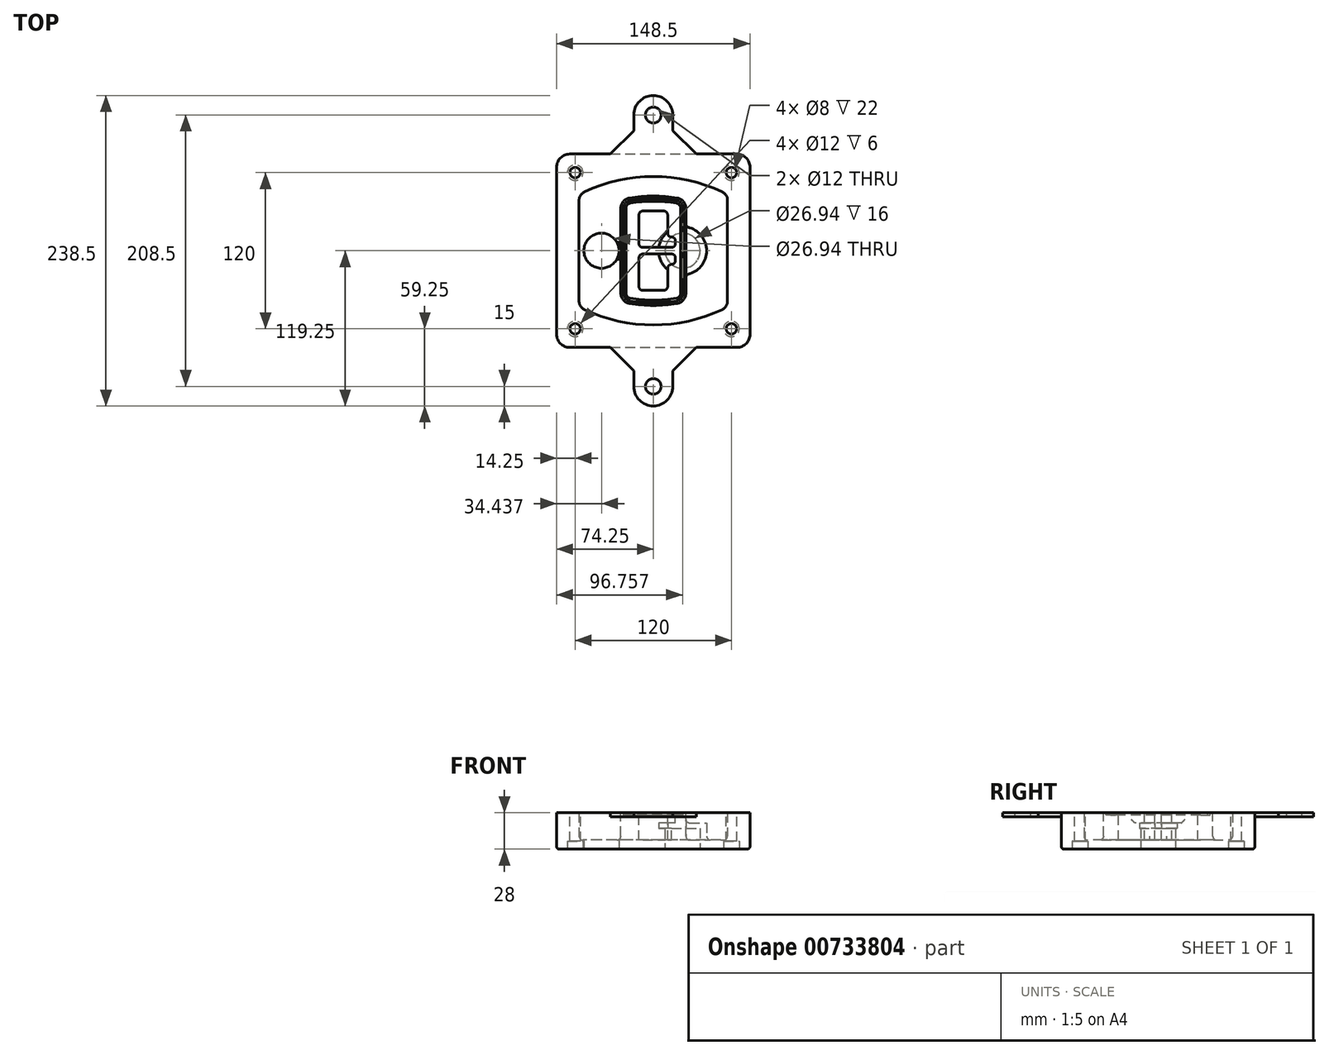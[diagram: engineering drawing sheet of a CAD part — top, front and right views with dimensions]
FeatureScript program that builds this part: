
annotation { "Feature Type Name" : "Feature", "Feature Type Description" : "" }
export const myFeature = defineFeature(function(context is Context, id is Id, definition is map)
    precondition{}
    {
        {
            var Q0;
            Q0=qCreatedBy(makeId("Top.planeOp"),FACE);
            var sketch = newSketch(context, id + "F0", { "sketchPlane" : qUnion([Q0])});
            skPoint(sketch, "E0.rect.middle", {"position": v(0, 0) * mm});
            skLineSegment(sketch, "E1.bottom", {"start": v(-64.25, -74.25) * mm, "end": v(64.25, -74.25) * mm});
            skLineSegment(sketch, "E1.top", {"start": v(-64.25, 74.25) * mm, "end": v(64.25, 74.25) * mm});
            skLineSegment(sketch, "E1.left", {"start": v(-74.25, -64.25) * mm, "end": v(-74.25, 64.25) * mm});
            skLineSegment(sketch, "E1.right", {"start": v(74.25, -64.25) * mm, "end": v(74.25, 64.25) * mm});
            skLineSegment(sketch, "E2", {"start": v(-74.25, 74.25) * mm, "end": v(74.25, -74.25) * mm, "construction": true});
            skLineSegment(sketch, "E3", {"start": v(74.25, 74.25) * mm, "end": v(-74.25, -74.25) * mm, "construction": true});
            skCircle(sketch, "E4", {"center": v(-60, 60) * mm, "radius": 4 * mm});
            skCircle(sketch, "E5", {"center": v(60, 60) * mm, "radius": 4 * mm});
            skCircle(sketch, "E6", {"center": v(60, -60) * mm, "radius": 4 * mm});
            skCircle(sketch, "E7", {"center": v(-60, -60) * mm, "radius": 4 * mm});
            skLineSegment(sketch, "E8", {"start": v(-60, 60) * mm, "end": v(60, 60) * mm, "construction": true});
            skLineSegment(sketch, "E9", {"start": v(60, 60) * mm, "end": v(60, -60) * mm, "construction": true});
            skLineSegment(sketch, "E10", {"start": v(60, -60) * mm, "end": v(-60, -60) * mm, "construction": true});
            skLineSegment(sketch, "E11", {"start": v(-60, -60) * mm, "end": v(-60, 60) * mm, "construction": true});
            skLineSegment(sketch, "E12", {"start": v(-60, 38.83) * mm, "end": v(-60, -38.83) * mm});
            skLineSegment(sketch, "E13", {"start": v(60, 38.83) * mm, "end": v(60, -38.83) * mm});
            skArc(sketch, "E14", {"start": v(54.26, 47.88) * mm, "mid": v(0, 60) * mm, "end": v(-54.26, 47.88) * mm});
            skArc(sketch, "E15", {"start": v(-54.26, -47.88) * mm, "mid": v(0, -60) * mm, "end": v(54.26, -47.88) * mm});
            skLineSegment(sketch, "E16", {"start": v(-60, 0) * mm, "end": v(60, 0) * mm, "construction": true});
            skPoint(sketch, "E17.visualSharp", {"position": v(-60, -45) * mm});
            skArc(sketch, "E17.filletArc", {"start": v(-60, -38.83) * mm, "mid": v(-58.44, -44.2) * mm, "end": v(-54.26, -47.88) * mm});
            skPoint(sketch, "E18.visualSharp", {"position": v(-60, 45) * mm});
            skArc(sketch, "E18.filletArc", {"start": v(-54.26, 47.88) * mm, "mid": v(-58.44, 44.2) * mm, "end": v(-60, 38.83) * mm});
            skPoint(sketch, "E19.visualSharp", {"position": v(60, 45) * mm});
            skArc(sketch, "E19.filletArc", {"start": v(60, 38.83) * mm, "mid": v(58.44, 44.2) * mm, "end": v(54.26, 47.88) * mm});
            skPoint(sketch, "E20.visualSharp", {"position": v(60, -45) * mm});
            skArc(sketch, "E20.filletArc", {"start": v(54.26, -47.88) * mm, "mid": v(58.44, -44.2) * mm, "end": v(60, -38.83) * mm});
            skPoint(sketch, "E21.visualSharp", {"position": v(-74.25, 74.25) * mm});
            skArc(sketch, "E21.filletArc", {"start": v(-64.25, 74.25) * mm, "mid": v(-71.32, 71.32) * mm, "end": v(-74.25, 64.25) * mm});
            skPoint(sketch, "E22.visualSharp", {"position": v(74.25, 74.25) * mm});
            skArc(sketch, "E22.filletArc", {"start": v(74.25, 64.25) * mm, "mid": v(71.32, 71.32) * mm, "end": v(64.25, 74.25) * mm});
            skPoint(sketch, "E23.visualSharp", {"position": v(74.25, -74.25) * mm});
            skArc(sketch, "E23.filletArc", {"start": v(64.25, -74.25) * mm, "mid": v(71.32, -71.32) * mm, "end": v(74.25, -64.25) * mm});
            skPoint(sketch, "E24.visualSharp", {"position": v(-74.25, -74.25) * mm});
            skArc(sketch, "E24.filletArc", {"start": v(-74.25, -64.25) * mm, "mid": v(-71.32, -71.32) * mm, "end": v(-64.25, -74.25) * mm});
            skArc(sketch, "E25.0", {"start": v(57, 38.83) * mm, "mid": v(55.9, 42.58) * mm, "end": v(52.98, 45.17) * mm});
            skLineSegment(sketch, "E25.1", {"start": v(57, 38.83) * mm, "end": v(57, -38.83) * mm});
            skArc(sketch, "E25.2", {"start": v(52.98, -45.17) * mm, "mid": v(55.9, -42.58) * mm, "end": v(57, -38.83) * mm});
            skArc(sketch, "E25.3", {"start": v(-52.98, -45.17) * mm, "mid": v(0, -57) * mm, "end": v(52.98, -45.17) * mm});
            skArc(sketch, "E25.4", {"start": v(-57, -38.83) * mm, "mid": v(-55.9, -42.58) * mm, "end": v(-52.98, -45.17) * mm});
            skArc(sketch, "E25.5", {"start": v(52.98, 45.17) * mm, "mid": v(0, 57) * mm, "end": v(-52.98, 45.17) * mm});
            skLineSegment(sketch, "E25.6", {"start": v(-57, 38.83) * mm, "end": v(-57, -38.83) * mm});
            skArc(sketch, "E25.7", {"start": v(-52.98, 45.17) * mm, "mid": v(-55.9, 42.58) * mm, "end": v(-57, 38.83) * mm});
            skArc(sketch, "E26.0", {"start": v(-55.96, 51.5) * mm, "mid": v(-61.82, 46.33) * mm, "end": v(-64, 38.83) * mm});
            skArc(sketch, "E26.1", {"start": v(55.96, 51.5) * mm, "mid": v(0, 64) * mm, "end": v(-55.96, 51.5) * mm});
            skArc(sketch, "E26.2", {"start": v(64, 38.83) * mm, "mid": v(61.82, 46.33) * mm, "end": v(55.96, 51.5) * mm});
            skLineSegment(sketch, "E26.3", {"start": v(64, 38.83) * mm, "end": v(64, -38.83) * mm});
            skArc(sketch, "E26.4", {"start": v(55.96, -51.5) * mm, "mid": v(61.82, -46.33) * mm, "end": v(64, -38.83) * mm});
            skLineSegment(sketch, "E26.5", {"start": v(-64, 38.83) * mm, "end": v(-64, -38.83) * mm});
            skArc(sketch, "E26.6", {"start": v(-55.96, -51.5) * mm, "mid": v(0, -64) * mm, "end": v(55.96, -51.5) * mm});
            skArc(sketch, "E26.7", {"start": v(-64, -38.83) * mm, "mid": v(-61.82, -46.33) * mm, "end": v(-55.96, -51.5) * mm});
            skSolve(sketch);
        }
        {
            var Q0;
            Q0=makeQuery(id+"F0.imprint","IMPRINT",FACE,{"disambiguationData":[TD([[makeQuery(id+"F0.imprint","IMPRINT",EDGE,{"derivedFrom":sQuery(id+"F0.wireOp",EDGE,"E1.bottom")}),1.0]])]});
            var Q1;
            Q1=makeQuery(id+"F0.imprint","IMPRINT",FACE,{"disambiguationData":[TD([[makeQuery(id+"F0.imprint","IMPRINT",EDGE,{"derivedFrom":sQuery(id+"F0.wireOp",EDGE,"E12")}),1.0]])]});
            var Q2;
            Q2=makeQuery(id+"F0.imprint","IMPRINT",FACE,{"disambiguationData":[TD([[makeQuery(id+"F0.imprint","IMPRINT",EDGE,{"derivedFrom":sQuery(id+"F0.wireOp",EDGE,"E25.0")}),1.0]])]});
            var Q3;
            Q3=makeQuery(id+"F0.imprint","IMPRINT",FACE,{"disambiguationData":[TD([[makeQuery(id+"F0.imprint","IMPRINT",EDGE,{"derivedFrom":sQuery(id+"F0.wireOp",EDGE,"E12")}),-1.0]])]});
            extrude(context, id + "F1", {"entities" : qUnion([Q0, Q1, Q2, Q3]), "oppositeDirection" : true, "depth" : 25 * mm});
        }
        {
            var Q0;
            Q0=makeQuery(id+"F0.imprint","IMPRINT",FACE,{"disambiguationData":[TD([[makeQuery(id+"F0.imprint","IMPRINT",EDGE,{"derivedFrom":sQuery(id+"F0.wireOp",EDGE,"E12")}),1.0]])]});
            extrude(context, id + "F2", {"entities" : qUnion([Q0]), "operationType" : NewBodyOperationType.ADD, "depth" : 3 * mm});
        }
        {
            var Q0;
            Q0=makeQuery(id+"F0.imprint","IMPRINT",FACE,{"disambiguationData":[TD([[makeQuery(id+"F0.imprint","IMPRINT",EDGE,{"derivedFrom":sQuery(id+"F0.wireOp",EDGE,"E25.0")}),1.0]])]});
            extrude(context, id + "F3", {"entities" : qUnion([Q0]), "operationType" : NewBodyOperationType.REMOVE, "oppositeDirection" : true, "depth" : 18 * mm});
        }
        {
            var Q0;
            Q0=makeQuery(id+"F2.opExtrude","CAP_FACE",FACE,{"disambiguationData":[OSD([sQuery(id+"F0.wireOp",EDGE,"E12"),sQuery(id+"F0.wireOp",EDGE,"E13"),sQuery(id+"F0.wireOp",EDGE,"E14"),sQuery(id+"F0.wireOp",EDGE,"E15"),sQuery(id+"F0.wireOp",EDGE,"E17.filletArc"),sQuery(id+"F0.wireOp",EDGE,"E18.filletArc"),sQuery(id+"F0.wireOp",EDGE,"E19.filletArc"),sQuery(id+"F0.wireOp",EDGE,"E20.filletArc"),sQuery(id+"F0.wireOp",EDGE,"E25.0"),sQuery(id+"F0.wireOp",EDGE,"E25.1"),sQuery(id+"F0.wireOp",EDGE,"E25.2"),sQuery(id+"F0.wireOp",EDGE,"E25.3"),sQuery(id+"F0.wireOp",EDGE,"E25.4"),sQuery(id+"F0.wireOp",EDGE,"E25.5"),sQuery(id+"F0.wireOp",EDGE,"E25.6"),sQuery(id+"F0.wireOp",EDGE,"E25.7")])],"isStart":false});
            var sketch = newSketch(context, id + "F4", { "sketchPlane" : qUnion([Q0])});
            skArc(sketch, "E27.0", {"start": v(-18.34, -40.45) * mm, "mid": v(0, -42) * mm, "end": v(18.34, -40.45) * mm});
            skArc(sketch, "E28.0", {"start": v(18.34, 40.45) * mm, "mid": v(0, 42) * mm, "end": v(-18.34, 40.45) * mm});
            skLineSegment(sketch, "E29", {"start": v(-25, 32.57) * mm, "end": v(-25, -32.57) * mm});
            skLineSegment(sketch, "E30", {"start": v(25, 32.57) * mm, "end": v(25, -32.57) * mm});
            skLineSegment(sketch, "E31", {"start": v(-25, 39.1) * mm, "end": v(25, 39.1) * mm, "construction": true});
            skLineSegment(sketch, "E32", {"start": v(-25, -39.1) * mm, "end": v(25, -39.1) * mm, "construction": true});
            skPoint(sketch, "E33.visualSharp", {"position": v(-25, 39.1) * mm});
            skArc(sketch, "E33.filletArc", {"start": v(-18.34, 40.45) * mm, "mid": v(-23.11, 37.73) * mm, "end": v(-25, 32.57) * mm});
            skPoint(sketch, "E34.visualSharp", {"position": v(25, 39.1) * mm});
            skArc(sketch, "E34.filletArc", {"start": v(25, 32.57) * mm, "mid": v(23.11, 37.73) * mm, "end": v(18.34, 40.45) * mm});
            skPoint(sketch, "E35.visualSharp", {"position": v(25, -39.1) * mm});
            skArc(sketch, "E35.filletArc", {"start": v(18.34, -40.45) * mm, "mid": v(23.11, -37.73) * mm, "end": v(25, -32.57) * mm});
            skPoint(sketch, "E36.visualSharp", {"position": v(-25, -39.1) * mm});
            skArc(sketch, "E36.filletArc", {"start": v(-25, -32.57) * mm, "mid": v(-23.11, -37.73) * mm, "end": v(-18.34, -40.45) * mm});
            skArc(sketch, "E37.0", {"start": v(52.98, 45.17) * mm, "mid": v(0, 57) * mm, "end": v(-52.98, 45.17) * mm});
            skArc(sketch, "E37.1", {"start": v(-52.98, 45.17) * mm, "mid": v(-55.9, 42.58) * mm, "end": v(-57, 38.83) * mm});
            skLineSegment(sketch, "E37.2", {"start": v(-57, 38.83) * mm, "end": v(-57, -38.83) * mm});
            skArc(sketch, "E37.3", {"start": v(-57, -38.83) * mm, "mid": v(-55.9, -42.58) * mm, "end": v(-52.98, -45.17) * mm});
            skArc(sketch, "E37.4", {"start": v(-52.98, -45.17) * mm, "mid": v(0, -57) * mm, "end": v(52.98, -45.17) * mm});
            skArc(sketch, "E37.5", {"start": v(52.98, -45.17) * mm, "mid": v(55.9, -42.58) * mm, "end": v(57, -38.83) * mm});
            skLineSegment(sketch, "E37.6", {"start": v(57, 38.83) * mm, "end": v(57, -38.83) * mm});
            skArc(sketch, "E37.7", {"start": v(57, 38.83) * mm, "mid": v(55.9, 42.58) * mm, "end": v(52.98, 45.17) * mm});
            skLineSegment(sketch, "E38.0", {"start": v(23, 32.57) * mm, "end": v(23, -32.57) * mm});
            skArc(sketch, "E38.1", {"start": v(18, -38.48) * mm, "mid": v(21.58, -36.44) * mm, "end": v(23, -32.57) * mm});
            skArc(sketch, "E38.2", {"start": v(-18, -38.48) * mm, "mid": v(0, -40) * mm, "end": v(18, -38.48) * mm});
            skArc(sketch, "E38.3", {"start": v(-23, -32.57) * mm, "mid": v(-21.58, -36.44) * mm, "end": v(-18, -38.48) * mm});
            skLineSegment(sketch, "E38.4", {"start": v(-23, 32.57) * mm, "end": v(-23, -32.57) * mm});
            skArc(sketch, "E38.5", {"start": v(23, 32.57) * mm, "mid": v(21.58, 36.44) * mm, "end": v(18, 38.48) * mm});
            skArc(sketch, "E38.6", {"start": v(-18, 38.48) * mm, "mid": v(-21.58, 36.44) * mm, "end": v(-23, 32.57) * mm});
            skArc(sketch, "E38.7", {"start": v(18, 38.48) * mm, "mid": v(0, 40) * mm, "end": v(-18, 38.48) * mm});
            skArc(sketch, "E39.0", {"start": v(21, 32.57) * mm, "mid": v(20.06, 35.15) * mm, "end": v(17.67, 36.5) * mm});
            skLineSegment(sketch, "E39.1", {"start": v(21, 32.57) * mm, "end": v(21, -32.57) * mm});
            skArc(sketch, "E39.2", {"start": v(17.67, -36.5) * mm, "mid": v(20.06, -35.15) * mm, "end": v(21, -32.57) * mm});
            skArc(sketch, "E39.3", {"start": v(-17.67, -36.5) * mm, "mid": v(0, -38) * mm, "end": v(17.67, -36.5) * mm});
            skArc(sketch, "E39.4", {"start": v(-21, -32.57) * mm, "mid": v(-20.06, -35.15) * mm, "end": v(-17.67, -36.5) * mm});
            skArc(sketch, "E39.5", {"start": v(17.67, 36.5) * mm, "mid": v(0, 38) * mm, "end": v(-17.67, 36.5) * mm});
            skLineSegment(sketch, "E39.6", {"start": v(-21, 32.57) * mm, "end": v(-21, -32.57) * mm});
            skArc(sketch, "E39.7", {"start": v(-17.67, 36.5) * mm, "mid": v(-20.06, 35.15) * mm, "end": v(-21, 32.57) * mm});
            skLineSegment(sketch, "E40", {"start": v(-25, 0) * mm, "end": v(25, 0) * mm, "construction": true});
            skLineSegment(sketch, "E41", {"start": v(-11, 5.5) * mm, "end": v(-11, 27.5) * mm});
            skLineSegment(sketch, "E42", {"start": v(-8, 30.5) * mm, "end": v(8, 30.5) * mm});
            skLineSegment(sketch, "E43", {"start": v(11, 27.5) * mm, "end": v(11, 13.5) * mm});
            skLineSegment(sketch, "E44", {"start": v(14, 10.5) * mm, "end": v(14, 10.5) * mm});
            skLineSegment(sketch, "E45", {"start": v(17, 7.5) * mm, "end": v(17, 5.5) * mm});
            skLineSegment(sketch, "E46", {"start": v(14, 2.5) * mm, "end": v(-8, 2.5) * mm});
            skPoint(sketch, "E47.visualSharp", {"position": v(-11, 30.5) * mm});
            skArc(sketch, "E47.filletArc", {"start": v(-8, 30.5) * mm, "mid": v(-10.12, 29.62) * mm, "end": v(-11, 27.5) * mm});
            skPoint(sketch, "E48.visualSharp", {"position": v(11, 30.5) * mm});
            skArc(sketch, "E48.filletArc", {"start": v(11, 27.5) * mm, "mid": v(10.12, 29.62) * mm, "end": v(8, 30.5) * mm});
            skPoint(sketch, "E49.visualSharp", {"position": v(11, 10.5) * mm});
            skArc(sketch, "E49.filletArc", {"start": v(11, 13.5) * mm, "mid": v(11.88, 11.38) * mm, "end": v(14, 10.5) * mm});
            skPoint(sketch, "E50.visualSharp", {"position": v(17, 10.5) * mm});
            skArc(sketch, "E50.filletArc", {"start": v(17, 7.5) * mm, "mid": v(16.12, 9.62) * mm, "end": v(14, 10.5) * mm});
            skPoint(sketch, "E51.visualSharp", {"position": v(17, 2.5) * mm});
            skArc(sketch, "E51.filletArc", {"start": v(14, 2.5) * mm, "mid": v(16.12, 3.38) * mm, "end": v(17, 5.5) * mm});
            skPoint(sketch, "E52.visualSharp", {"position": v(-11, 2.5) * mm});
            skArc(sketch, "E52.filletArc", {"start": v(-11, 5.5) * mm, "mid": v(-10.12, 3.38) * mm, "end": v(-8, 2.5) * mm});
            skLineSegment(sketch, "E53.0.MirrorCS", {"start": v(14, -2.5) * mm, "end": v(-8, -2.5) * mm});
            skArc(sketch, "E54.0.MirrorCS", {"start": v(-11, -5.5) * mm, "mid": v(-10.12, -3.38) * mm, "end": v(-8, -2.5) * mm});
            skLineSegment(sketch, "E55.0.MirrorCS", {"start": v(-11, -5.5) * mm, "end": v(-11, -27.5) * mm});
            skArc(sketch, "E56.0.MirrorCS", {"start": v(-8, -30.5) * mm, "mid": v(-10.12, -29.62) * mm, "end": v(-11, -27.5) * mm});
            skLineSegment(sketch, "E57.0.MirrorCS", {"start": v(-8, -30.5) * mm, "end": v(8, -30.5) * mm});
            skArc(sketch, "E58.0.MirrorCS", {"start": v(11, -27.5) * mm, "mid": v(10.12, -29.62) * mm, "end": v(8, -30.5) * mm});
            skLineSegment(sketch, "E59.0.MirrorCS", {"start": v(11, -27.5) * mm, "end": v(11, -13.5) * mm});
            skArc(sketch, "E60.0.MirrorCS", {"start": v(11, -13.5) * mm, "mid": v(11.88, -11.38) * mm, "end": v(14, -10.5) * mm});
            skArc(sketch, "E61.0.MirrorCS", {"start": v(17, -7.5) * mm, "mid": v(16.12, -9.62) * mm, "end": v(14, -10.5) * mm});
            skLineSegment(sketch, "E62.0.MirrorCS", {"start": v(17, -7.5) * mm, "end": v(17, -5.5) * mm});
            skArc(sketch, "E63.0.MirrorCS", {"start": v(14, -2.5) * mm, "mid": v(16.12, -3.38) * mm, "end": v(17, -5.5) * mm});
            skSolve(sketch);
        }
        {
            var Q0;
            Q0=makeQuery(id+"F4.imprint","IMPRINT",FACE,{"disambiguationData":[TD([[makeQuery(id+"F4.imprint","IMPRINT",EDGE,{"derivedFrom":sQuery(id+"F4.wireOp",EDGE,"E27.0")}),1.0]])]});
            var Q1;
            Q1=makeQuery(id+"F4.imprint","IMPRINT",FACE,{"disambiguationData":[TD([[makeQuery(id+"F4.imprint","IMPRINT",EDGE,{"derivedFrom":sQuery(id+"F4.wireOp",EDGE,"E38.0")}),-1.0]])]});
            var Q2;
            Q2=makeQuery(id+"F4.imprint","IMPRINT",FACE,{"disambiguationData":[TD([[makeQuery(id+"F4.imprint","IMPRINT",EDGE,{"derivedFrom":sQuery(id+"F4.wireOp",EDGE,"E39.0")}),1.0]])]});
            extrude(context, id + "F5", {"entities" : qUnion([Q0, Q1, Q2]), "operationType" : NewBodyOperationType.ADD, "endBound" : BoundingType.UP_TO_NEXT, "oppositeDirection" : true, "depth" : 25 * mm});
        }
        {
            var Q0;
            Q0=makeQuery(id+"F4.imprint","IMPRINT",FACE,{"disambiguationData":[TD([[makeQuery(id+"F4.imprint","IMPRINT",EDGE,{"derivedFrom":sQuery(id+"F4.wireOp",EDGE,"E38.0")}),-1.0]])]});
            extrude(context, id + "F6", {"entities" : qUnion([Q0]), "operationType" : NewBodyOperationType.REMOVE, "oppositeDirection" : true, "depth" : 2 * mm});
        }
        {
            var Q0;
            Q0=makeQuery(id+"F1.opExtrude","CAP_FACE",FACE,{"disambiguationData":[OSD([sQuery(id+"F0.wireOp",EDGE,"E1.bottom"),sQuery(id+"F0.wireOp",EDGE,"E1.top"),sQuery(id+"F0.wireOp",EDGE,"E1.left"),sQuery(id+"F0.wireOp",EDGE,"E1.right"),sQuery(id+"F0.wireOp",EDGE,"E4"),sQuery(id+"F0.wireOp",EDGE,"E5"),sQuery(id+"F0.wireOp",EDGE,"E6"),sQuery(id+"F0.wireOp",EDGE,"E7"),sQuery(id+"F0.wireOp",EDGE,"E21.filletArc"),sQuery(id+"F0.wireOp",EDGE,"E22.filletArc"),sQuery(id+"F0.wireOp",EDGE,"E23.filletArc"),sQuery(id+"F0.wireOp",EDGE,"E24.filletArc")])],"isStart":false});
            var sketch = newSketch(context, id + "F7", { "sketchPlane" : qUnion([Q0])});
            skCircle(sketch, "E64", {"center": v(22.5, 0) * mm, "radius": 13.47 * mm});
            skCircle(sketch, "E65", {"center": v(-39.81, 0) * mm, "radius": 13.47 * mm});
            skLineSegment(sketch, "E66", {"start": v(74.25, 0) * mm, "end": v(-74.25, 0) * mm});
            skCircle(sketch, "E67", {"center": v(22.5, 0) * mm, "radius": 18.47 * mm});
            skCircle(sketch, "E68", {"center": v(60, -60) * mm, "radius": 6 * mm});
            skCircle(sketch, "E69", {"center": v(-60, -60) * mm, "radius": 6 * mm});
            skCircle(sketch, "E70", {"center": v(-60, 60) * mm, "radius": 6 * mm});
            skCircle(sketch, "E71", {"center": v(60, 60) * mm, "radius": 6 * mm});
            skSolve(sketch);
        }
        {
            var Q0;
            {var subQ1=sQuery(id+"F7.wireOp",EDGE,"E66");var subQ4=sQuery(id+"F7.wireOp",EDGE,"E64");var subQ6=makeQuery(id+"F7.imprint","INTERSECT",VERTEX,{"disambiguationData":[OD(0.0)],"derivedFrom":[subQ4,subQ1]});Q0=makeQuery(id+"F7.imprint","IMPRINT",FACE,{"disambiguationData":[TD([[makeQuery(id+"F7.imprint","IMPRINT",EDGE,{"disambiguationData":[TD([[subQ6,-1.0]])],"derivedFrom":subQ4}),-1.0]])]});}
            var Q1;
            {var subQ0=sQuery(id+"F7.wireOp",EDGE,"E66");var subQ1=sQuery(id+"F7.wireOp",EDGE,"E64");var subQ3=makeQuery(id+"F7.imprint","INTERSECT",VERTEX,{"disambiguationData":[OD(0.0)],"derivedFrom":[subQ1,subQ0]});Q1=makeQuery(id+"F7.imprint","IMPRINT",FACE,{"disambiguationData":[TD([[makeQuery(id+"F7.imprint","IMPRINT",EDGE,{"disambiguationData":[TD([[subQ3,-1.0]])],"derivedFrom":subQ1}),1.0]])]});}
            var Q2;
            {var subQ0=sQuery(id+"F7.wireOp",EDGE,"E66");var subQ1=sQuery(id+"F7.wireOp",EDGE,"E64");var subQ3=makeQuery(id+"F7.imprint","INTERSECT",VERTEX,{"disambiguationData":[OD(0.0)],"derivedFrom":[subQ1,subQ0]});Q2=makeQuery(id+"F7.imprint","IMPRINT",FACE,{"disambiguationData":[TD([[makeQuery(id+"F7.imprint","IMPRINT",EDGE,{"disambiguationData":[TD([[subQ3,1.0]])],"derivedFrom":subQ1}),1.0]])]});}
            var Q3;
            {var subQ1=sQuery(id+"F7.wireOp",EDGE,"E66");var subQ4=sQuery(id+"F7.wireOp",EDGE,"E64");var subQ6=makeQuery(id+"F7.imprint","INTERSECT",VERTEX,{"disambiguationData":[OD(0.0)],"derivedFrom":[subQ4,subQ1]});Q3=makeQuery(id+"F7.imprint","IMPRINT",FACE,{"disambiguationData":[TD([[makeQuery(id+"F7.imprint","IMPRINT",EDGE,{"disambiguationData":[TD([[subQ6,1.0]])],"derivedFrom":subQ4}),-1.0]])]});}
            extrude(context, id + "F8", {"entities" : qUnion([Q0, Q1, Q2, Q3]), "operationType" : NewBodyOperationType.ADD, "oppositeDirection" : true, "depth" : 20 * mm});
        }
        {
            var Q0;
            {var subQ0=sQuery(id+"F7.wireOp",EDGE,"E66");var subQ1=sQuery(id+"F7.wireOp",EDGE,"E64");var subQ3=makeQuery(id+"F7.imprint","INTERSECT",VERTEX,{"disambiguationData":[OD(0.0)],"derivedFrom":[subQ1,subQ0]});Q0=makeQuery(id+"F7.imprint","IMPRINT",FACE,{"disambiguationData":[TD([[makeQuery(id+"F7.imprint","IMPRINT",EDGE,{"disambiguationData":[TD([[subQ3,-1.0]])],"derivedFrom":subQ1}),1.0]])]});}
            var Q1;
            {var subQ0=sQuery(id+"F7.wireOp",EDGE,"E66");var subQ1=sQuery(id+"F7.wireOp",EDGE,"E64");var subQ3=makeQuery(id+"F7.imprint","INTERSECT",VERTEX,{"disambiguationData":[OD(0.0)],"derivedFrom":[subQ1,subQ0]});Q1=makeQuery(id+"F7.imprint","IMPRINT",FACE,{"disambiguationData":[TD([[makeQuery(id+"F7.imprint","IMPRINT",EDGE,{"disambiguationData":[TD([[subQ3,1.0]])],"derivedFrom":subQ1}),1.0]])]});}
            extrude(context, id + "F9", {"entities" : qUnion([Q0, Q1]), "operationType" : NewBodyOperationType.REMOVE, "oppositeDirection" : true, "depth" : 16 * mm});
        }
        {
            var Q0;
            {var subQ0=sQuery(id+"F7.wireOp",EDGE,"E66");var subQ1=sQuery(id+"F7.wireOp",EDGE,"E65");var subQ3=makeQuery(id+"F7.imprint","INTERSECT",VERTEX,{"disambiguationData":[OD(0.0)],"derivedFrom":[subQ1,subQ0]});Q0=makeQuery(id+"F7.imprint","IMPRINT",FACE,{"disambiguationData":[TD([[makeQuery(id+"F7.imprint","IMPRINT",EDGE,{"disambiguationData":[TD([[subQ3,-1.0]])],"derivedFrom":subQ1}),1.0]])]});}
            var Q1;
            {var subQ0=sQuery(id+"F7.wireOp",EDGE,"E66");var subQ1=sQuery(id+"F7.wireOp",EDGE,"E65");var subQ3=makeQuery(id+"F7.imprint","INTERSECT",VERTEX,{"disambiguationData":[OD(0.0)],"derivedFrom":[subQ1,subQ0]});Q1=makeQuery(id+"F7.imprint","IMPRINT",FACE,{"disambiguationData":[TD([[makeQuery(id+"F7.imprint","IMPRINT",EDGE,{"disambiguationData":[TD([[subQ3,1.0]])],"derivedFrom":subQ1}),1.0]])]});}
            extrude(context, id + "F10", {"entities" : qUnion([Q0, Q1]), "operationType" : NewBodyOperationType.REMOVE, "oppositeDirection" : true, "depth" : 25 * mm});
        }
        {
            var Q0;
            Q0=makeQuery(id+"F7.imprint","IMPRINT",FACE,{"disambiguationData":[TD([[makeQuery(id+"F7.imprint","IMPRINT",EDGE,{"derivedFrom":sQuery(id+"F7.wireOp",EDGE,"E68")}),1.0]])]});
            var Q1;
            Q1=makeQuery(id+"F7.imprint","IMPRINT",FACE,{"disambiguationData":[TD([[makeQuery(id+"F7.imprint","IMPRINT",EDGE,{"derivedFrom":makeQuery(id+"F1.opExtrude","CAP_EDGE",EDGE,{"disambiguationData":[OSD([sQuery(id+"F0.wireOp",EDGE,"E5")])],"isStart":false})}),-1.0]])]});
            var Q2;
            Q2=makeQuery(id+"F7.imprint","IMPRINT",FACE,{"disambiguationData":[TD([[makeQuery(id+"F7.imprint","IMPRINT",EDGE,{"derivedFrom":sQuery(id+"F7.wireOp",EDGE,"E69")}),1.0]])]});
            var Q3;
            Q3=makeQuery(id+"F7.imprint","IMPRINT",FACE,{"disambiguationData":[TD([[makeQuery(id+"F7.imprint","IMPRINT",EDGE,{"derivedFrom":makeQuery(id+"F1.opExtrude","CAP_EDGE",EDGE,{"disambiguationData":[OSD([sQuery(id+"F0.wireOp",EDGE,"E4")])],"isStart":false})}),-1.0]])]});
            var Q4;
            Q4=makeQuery(id+"F7.imprint","IMPRINT",FACE,{"disambiguationData":[TD([[makeQuery(id+"F7.imprint","IMPRINT",EDGE,{"derivedFrom":sQuery(id+"F7.wireOp",EDGE,"E70")}),1.0]])]});
            var Q5;
            Q5=makeQuery(id+"F7.imprint","IMPRINT",FACE,{"disambiguationData":[TD([[makeQuery(id+"F7.imprint","IMPRINT",EDGE,{"derivedFrom":makeQuery(id+"F1.opExtrude","CAP_EDGE",EDGE,{"disambiguationData":[OSD([sQuery(id+"F0.wireOp",EDGE,"E7")])],"isStart":false})}),-1.0]])]});
            var Q6;
            Q6=makeQuery(id+"F7.imprint","IMPRINT",FACE,{"disambiguationData":[TD([[makeQuery(id+"F7.imprint","IMPRINT",EDGE,{"derivedFrom":sQuery(id+"F7.wireOp",EDGE,"E71")}),1.0]])]});
            var Q7;
            Q7=makeQuery(id+"F7.imprint","IMPRINT",FACE,{"disambiguationData":[TD([[makeQuery(id+"F7.imprint","IMPRINT",EDGE,{"derivedFrom":makeQuery(id+"F1.opExtrude","CAP_EDGE",EDGE,{"disambiguationData":[OSD([sQuery(id+"F0.wireOp",EDGE,"E6")])],"isStart":false})}),-1.0]])]});
            extrude(context, id + "F11", {"entities" : qUnion([Q0, Q1, Q2, Q3, Q4, Q5, Q6, Q7]), "operationType" : NewBodyOperationType.REMOVE, "oppositeDirection" : true, "depth" : 6 * mm});
        }
        {
            var Q0;
            Q0=makeQuery(id+"F9.boolean.opBoolean","COPY",FACE,{"derivedFrom":makeQuery(id+"F9.opExtrude","CAP_FACE",FACE,{"disambiguationData":[OSD([sQuery(id+"F7.wireOp",EDGE,"E64")])],"isStart":false})});
            var sketch = newSketch(context, id + "F12", { "sketchPlane" : qUnion([Q0])});
            skArc(sketch, "E72.0", {"start": v(11, 14.45) * mm, "mid": v(6.45, 9.13) * mm, "end": v(4.2, 2.5) * mm});
            skArc(sketch, "E72.1", {"start": v(4.2, -2.5) * mm, "mid": v(6.45, -9.13) * mm, "end": v(11, -14.45) * mm});
            skLineSegment(sketch, "E73", {"start": v(4.2, -2.5) * mm, "end": v(14, -2.5) * mm});
            skLineSegment(sketch, "E74.0", {"start": v(14, 2.5) * mm, "end": v(4.2, 2.5) * mm});
            skArc(sketch, "E74.1", {"start": v(14, 2.5) * mm, "mid": v(16.12, 3.38) * mm, "end": v(17, 5.5) * mm});
            skLineSegment(sketch, "E74.2", {"start": v(17, 7.5) * mm, "end": v(17, 5.5) * mm});
            skArc(sketch, "E74.3", {"start": v(17, 7.5) * mm, "mid": v(16.12, 9.62) * mm, "end": v(14, 10.5) * mm});
            skArc(sketch, "E74.4", {"start": v(11, 13.5) * mm, "mid": v(11.88, 11.38) * mm, "end": v(14, 10.5) * mm});
            skLineSegment(sketch, "E74.5", {"start": v(11, 14.45) * mm, "end": v(11, 13.5) * mm});
            skLineSegment(sketch, "E74.7", {"start": v(14, -2.5) * mm, "end": v(4.2, -2.5) * mm});
            skArc(sketch, "E74.8", {"start": v(14, -2.5) * mm, "mid": v(16.12, -3.38) * mm, "end": v(17, -5.5) * mm});
            skLineSegment(sketch, "E74.9", {"start": v(17, -7.5) * mm, "end": v(17, -5.5) * mm});
            skArc(sketch, "E74.10", {"start": v(17, -7.5) * mm, "mid": v(16.12, -9.62) * mm, "end": v(14, -10.5) * mm});
            skArc(sketch, "E74.11", {"start": v(11, -13.5) * mm, "mid": v(11.88, -11.38) * mm, "end": v(14, -10.5) * mm});
            skLineSegment(sketch, "E74.12", {"start": v(11, -14.45) * mm, "end": v(11, -13.5) * mm});
            skPoint(sketch, "E75.orphan", {"position": v(11, -27.5) * mm});
            skPoint(sketch, "E76.orphan", {"position": v(-8, -2.5) * mm});
            skPoint(sketch, "E77.orphan", {"position": v(-8, 2.5) * mm});
            skPoint(sketch, "E78.orphan", {"position": v(11, 27.5) * mm});
            skSolve(sketch);
        }
        {
            var Q0;
            {var subQ7=sQuery(id+"F12.wireOp",EDGE,"E72.0");var subQ14=sQuery(id+"F12.wireOp",EDGE,"E72.1");var subQ16=sQuery(id+"F12.wireOp",EDGE,"E74.1");var subQ18=sQuery(id+"F12.wireOp",EDGE,"E74.8");Q0=qUnion([makeQuery(id+"F12.imprint","IMPRINT",FACE,{"disambiguationData":[TD([[makeQuery(id+"F12.imprint","IMPRINT",EDGE,{"derivedFrom":subQ7}),1.0]])]}),makeQuery(id+"F12.imprint","IMPRINT",FACE,{"disambiguationData":[TD([[makeQuery(id+"F12.imprint","IMPRINT",EDGE,{"derivedFrom":subQ14}),1.0]])]}),makeQuery(id+"F12.imprint","IMPRINT",FACE,{"disambiguationData":[TD([[makeQuery(id+"F12.imprint","IMPRINT",EDGE,{"derivedFrom":subQ16}),1.0]])]}),makeQuery(id+"F12.imprint","IMPRINT",FACE,{"disambiguationData":[TD([[makeQuery(id+"F12.imprint","IMPRINT",EDGE,{"derivedFrom":subQ18}),-1.0]])]})]);}
            var Q1;
            Q1=makeQuery(id+"F5.boolean.opBoolean","SPLIT",FACE,{"disambiguationData":[TD([makeQuery(id+"F5.opExtrude","SWEPT_FACE",FACE,{"disambiguationData":[OSD([sQuery(id+"F4.wireOp",EDGE,"E41")])]})])],"derivedFrom":makeQuery(id+"F3.boolean.opBoolean","COPY",FACE,{"derivedFrom":makeQuery(id+"F3.opExtrude","CAP_FACE",FACE,{"disambiguationData":[OSD([sQuery(id+"F0.wireOp",EDGE,"E25.0"),sQuery(id+"F0.wireOp",EDGE,"E25.1"),sQuery(id+"F0.wireOp",EDGE,"E25.2"),sQuery(id+"F0.wireOp",EDGE,"E25.3"),sQuery(id+"F0.wireOp",EDGE,"E25.4"),sQuery(id+"F0.wireOp",EDGE,"E25.5"),sQuery(id+"F0.wireOp",EDGE,"E25.6"),sQuery(id+"F0.wireOp",EDGE,"E25.7")])],"isStart":false})})});
            extrude(context, id + "F13", {"entities" : qUnion([Q0]), "operationType" : NewBodyOperationType.REMOVE, "endBound" : BoundingType.UP_TO_SURFACE, "endBoundEntityFace" : qUnion([Q1]), "depth" : 25 * mm});
        }
        {
            var Q0;
            Q0=makeQuery(id+"F3.boolean.opBoolean","COPY",EDGE,{"derivedFrom":makeQuery(id+"F3.opExtrude","CAP_EDGE",EDGE,{"disambiguationData":[OSD([sQuery(id+"F0.wireOp",EDGE,"E25.6")])],"isStart":false})});
            var Q1;
            Q1=makeQuery(id+"F8.boolean.opBoolean","INTERSECT",EDGE,{"derivedFrom":[makeQuery(id+"F5.opExtrude","SWEPT_FACE",FACE,{"disambiguationData":[OSD([sQuery(id+"F4.wireOp",EDGE,"E30")])]}),makeQuery(id+"F8.opExtrude","CAP_FACE",FACE,{"disambiguationData":[OSD([sQuery(id+"F7.wireOp",EDGE,"E67")])],"isStart":false})]});
            var Q2;
            Q2=makeQuery(id+"F8.boolean.opBoolean","INTERSECT",EDGE,{"disambiguationData":[OD(1.0)],"derivedFrom":[makeQuery(id+"F5.opExtrude","SWEPT_FACE",FACE,{"disambiguationData":[OSD([sQuery(id+"F4.wireOp",EDGE,"E30")])]}),makeQuery(id+"F8.opExtrude","SWEPT_FACE",FACE,{"disambiguationData":[OSD([sQuery(id+"F7.wireOp",EDGE,"E67")])]})]});
            var Q3;
            {var subQ0=sQuery(id+"F4.wireOp",EDGE,"E30");Q3=makeQuery(id+"F8.boolean.opBoolean","SPLIT",EDGE,{"disambiguationData":[TD([makeQuery(id+"F5.opExtrude","SWEPT_FACE",FACE,{"disambiguationData":[OSD([sQuery(id+"F4.wireOp",EDGE,"E35.filletArc")])]})])],"derivedFrom":makeQuery(id+"F5.opExtrude","CAP_EDGE",EDGE,{"disambiguationData":[OSD([subQ0])],"isStart":false})});}
            var Q4;
            {var subQ0=sQuery(id+"F0.wireOp",EDGE,"E25.7");var subQ1=sQuery(id+"F0.wireOp",EDGE,"E25.1");var subQ2=sQuery(id+"F0.wireOp",EDGE,"E25.6");var subQ3=sQuery(id+"F0.wireOp",EDGE,"E25.5");var subQ4=sQuery(id+"F0.wireOp",EDGE,"E25.4");var subQ5=sQuery(id+"F0.wireOp",EDGE,"E25.0");var subQ6=sQuery(id+"F0.wireOp",EDGE,"E25.2");var subQ7=sQuery(id+"F0.wireOp",EDGE,"E25.3");Q4=makeQuery(id+"F8.boolean.opBoolean","INTERSECT",EDGE,{"derivedFrom":[makeQuery(id+"F5.boolean.opBoolean","SPLIT",FACE,{"disambiguationData":[TD([makeQuery(id+"F2.opExtrude","SWEPT_FACE",FACE,{"disambiguationData":[OSD([subQ5])]})])],"derivedFrom":makeQuery(id+"F3.boolean.opBoolean","COPY",FACE,{"derivedFrom":makeQuery(id+"F3.opExtrude","CAP_FACE",FACE,{"disambiguationData":[OSD([subQ5,subQ1,subQ6,subQ7,subQ4,subQ3,subQ2,subQ0])],"isStart":false})})}),makeQuery(id+"F8.opExtrude","SWEPT_FACE",FACE,{"disambiguationData":[OSD([sQuery(id+"F7.wireOp",EDGE,"E67")])]})]});}
            var Q5;
            Q5=makeQuery(id+"F8.boolean.opBoolean","INTERSECT",EDGE,{"disambiguationData":[OD(0.0)],"derivedFrom":[makeQuery(id+"F5.opExtrude","SWEPT_FACE",FACE,{"disambiguationData":[OSD([sQuery(id+"F4.wireOp",EDGE,"E30")])]}),makeQuery(id+"F8.opExtrude","SWEPT_FACE",FACE,{"disambiguationData":[OSD([sQuery(id+"F7.wireOp",EDGE,"E67")])]})]});
            fillet(context, id + "F14", {"entities" : qUnion([Q0, Q1, Q2, Q3, Q4, Q5]), "radius" : 3 * mm, "tangentPropagation" : true, "allowEdgeOverflow" : false});
        }
        {
            var Q0;
            Q0=makeQuery(id+"F1.opExtrude","CAP_EDGE",EDGE,{"disambiguationData":[OSD([sQuery(id+"F0.wireOp",EDGE,"E1.bottom")])],"isStart":false});
            fillet(context, id + "F15", {"entities" : qUnion([Q0]), "radius" : 2 * mm, "tangentPropagation" : true, "allowEdgeOverflow" : false});
        }
        {
            var Q0;
            {var subQ0=sQuery(id+"F0.wireOp",EDGE,"E21.filletArc");var subQ1=sQuery(id+"F0.wireOp",EDGE,"E7");var subQ2=sQuery(id+"F0.wireOp",EDGE,"E6");var subQ3=sQuery(id+"F0.wireOp",EDGE,"E5");var subQ4=sQuery(id+"F0.wireOp",EDGE,"E4");var subQ5=sQuery(id+"F0.wireOp",EDGE,"E22.filletArc");var subQ6=sQuery(id+"F0.wireOp",EDGE,"E1.bottom");var subQ7=sQuery(id+"F0.wireOp",EDGE,"E1.right");var subQ8=sQuery(id+"F0.wireOp",EDGE,"E1.top");var subQ9=sQuery(id+"F0.wireOp",EDGE,"E1.left");var subQ10=sQuery(id+"F0.wireOp",EDGE,"E23.filletArc");var subQ11=sQuery(id+"F0.wireOp",EDGE,"E24.filletArc");Q0=makeQuery(id+"F2.boolean.opBoolean","SPLIT",FACE,{"disambiguationData":[TD([makeQuery(id+"F1.opExtrude","SWEPT_FACE",FACE,{"disambiguationData":[OSD([subQ6])]})])],"derivedFrom":makeQuery(id+"F1.opExtrude","CAP_FACE",FACE,{"disambiguationData":[OSD([subQ6,subQ8,subQ9,subQ7,subQ4,subQ3,subQ2,subQ1,subQ0,subQ5,subQ10,subQ11])],"isStart":true})});}
            var sketch = newSketch(context, id + "F16", { "sketchPlane" : qUnion([Q0])});
            skLineSegment(sketch, "E79", {"start": v(0, 74.25) * mm, "end": v(0, 107.95) * mm, "construction": true});
            skLineSegment(sketch, "E80", {"start": v(-33, 74.25) * mm, "end": v(-15, 92.25) * mm});
            skLineSegment(sketch, "E81", {"start": v(-15, 92.25) * mm, "end": v(-15, 104.25) * mm});
            skLineSegment(sketch, "E82.MirrorCS", {"start": v(33, 74.25) * mm, "end": v(15, 92.25) * mm});
            skLineSegment(sketch, "E83.MirrorCS", {"start": v(15, 92.25) * mm, "end": v(15, 104.25) * mm});
            skArc(sketch, "E84", {"start": v(15, 104.25) * mm, "mid": v(0, 119.25) * mm, "end": v(-15, 104.25) * mm});
            skPoint(sketch, "E84.centerSnap0", {"position": v(0, 91.1) * mm});
            skCircle(sketch, "E85", {"center": v(0, 104.25) * mm, "radius": 6 * mm});
            skLineSegment(sketch, "E86", {"start": v(-74.25, 0) * mm, "end": v(87.02, 0) * mm, "construction": true});
            skPoint(sketch, "E86.endSnap0", {"position": v(60, 0) * mm});
            skLineSegment(sketch, "E87.MirrorCS", {"start": v(33, -74.25) * mm, "end": v(15, -92.25) * mm});
            skLineSegment(sketch, "E88.MirrorCS", {"start": v(15, -92.25) * mm, "end": v(15, -104.25) * mm});
            skArc(sketch, "E89.MirrorCS", {"start": v(15, -104.25) * mm, "mid": v(0, -119.25) * mm, "end": v(-15, -104.25) * mm});
            skCircle(sketch, "E90.MirrorC", {"center": v(0, -104.25) * mm, "radius": 6 * mm});
            skLineSegment(sketch, "E91.MirrorCS", {"start": v(-15, -92.25) * mm, "end": v(-15, -104.25) * mm});
            skLineSegment(sketch, "E92.MirrorCS", {"start": v(-33, -74.25) * mm, "end": v(-15, -92.25) * mm});
            skSolve(sketch);
        }
        {
            var Q0;
            {var subQ0=sQuery(id+"F16.wireOp",EDGE,"E87.MirrorCS");Q0=makeQuery(id+"F16.imprint","IMPRINT",FACE,{"disambiguationData":[TD([[makeQuery(id+"F16.imprint","IMPRINT",EDGE,{"derivedFrom":subQ0}),-1.0]])]});}
            var Q1;
            {var subQ1=sQuery(id+"F16.wireOp",EDGE,"E80");Q1=makeQuery(id+"F16.imprint","IMPRINT",FACE,{"disambiguationData":[TD([[makeQuery(id+"F16.imprint","IMPRINT",EDGE,{"derivedFrom":subQ1}),-1.0]])]});}
            var Q2;
            Q2=makeQuery(id+"F16.imprint","IMPRINT",FACE,{"disambiguationData":[TD([[makeQuery(id+"F16.imprint","IMPRINT",EDGE,{"derivedFrom":makeQuery(id+"F1.opExtrude","CAP_EDGE",EDGE,{"disambiguationData":[OSD([sQuery(id+"F0.wireOp",EDGE,"E1.left")])],"isStart":true})}),-1.0]])]});
            var Q3;
            Q3=makeQuery(id+"F2.opExtrude","CAP_FACE",FACE,{"disambiguationData":[OSD([sQuery(id+"F0.wireOp",EDGE,"E12"),sQuery(id+"F0.wireOp",EDGE,"E13"),sQuery(id+"F0.wireOp",EDGE,"E14"),sQuery(id+"F0.wireOp",EDGE,"E15"),sQuery(id+"F0.wireOp",EDGE,"E17.filletArc"),sQuery(id+"F0.wireOp",EDGE,"E18.filletArc"),sQuery(id+"F0.wireOp",EDGE,"E19.filletArc"),sQuery(id+"F0.wireOp",EDGE,"E20.filletArc"),sQuery(id+"F0.wireOp",EDGE,"E25.0"),sQuery(id+"F0.wireOp",EDGE,"E25.1"),sQuery(id+"F0.wireOp",EDGE,"E25.2"),sQuery(id+"F0.wireOp",EDGE,"E25.3"),sQuery(id+"F0.wireOp",EDGE,"E25.4"),sQuery(id+"F0.wireOp",EDGE,"E25.5"),sQuery(id+"F0.wireOp",EDGE,"E25.6"),sQuery(id+"F0.wireOp",EDGE,"E25.7")])],"isStart":false});
            var Q4;
            Q4=makeQuery(id+"F1.opExtrude","SWEPT_BODY",BODY,{"disambiguationData":[OSD([sQuery(id+"F0.wireOp",EDGE,"E1.bottom"),sQuery(id+"F0.wireOp",EDGE,"E1.top"),sQuery(id+"F0.wireOp",EDGE,"E1.left"),sQuery(id+"F0.wireOp",EDGE,"E1.right"),sQuery(id+"F0.wireOp",EDGE,"E4"),sQuery(id+"F0.wireOp",EDGE,"E5"),sQuery(id+"F0.wireOp",EDGE,"E6"),sQuery(id+"F0.wireOp",EDGE,"E7"),sQuery(id+"F0.wireOp",EDGE,"E21.filletArc"),sQuery(id+"F0.wireOp",EDGE,"E22.filletArc"),sQuery(id+"F0.wireOp",EDGE,"E23.filletArc"),sQuery(id+"F0.wireOp",EDGE,"E24.filletArc")])]});
            var Q5;
            Q5=makeQuery(id+"F2.opExtrude","CAP_VERTEX",VERTEX,{"disambiguationData":[OSD([sQuery(id+"F0.wireOp",EDGE,"E25.4"),sQuery(id+"F0.wireOp",EDGE,"E25.6")])],"isStart":false});
            extrude(context, id + "F17", {"entities" : qUnion([Q0, Q1, Q2]), "operationType" : NewBodyOperationType.ADD, "endBound" : BoundingType.UP_TO_VERTEX, "depth" : 25 * mm, "endBoundEntityFace" : qUnion([Q3]), "endBoundEntityBody" : qUnion([Q4]), "endBoundEntityVertex" : qUnion([Q5]), "offsetDistance" : 25 * mm});
        }
    });
